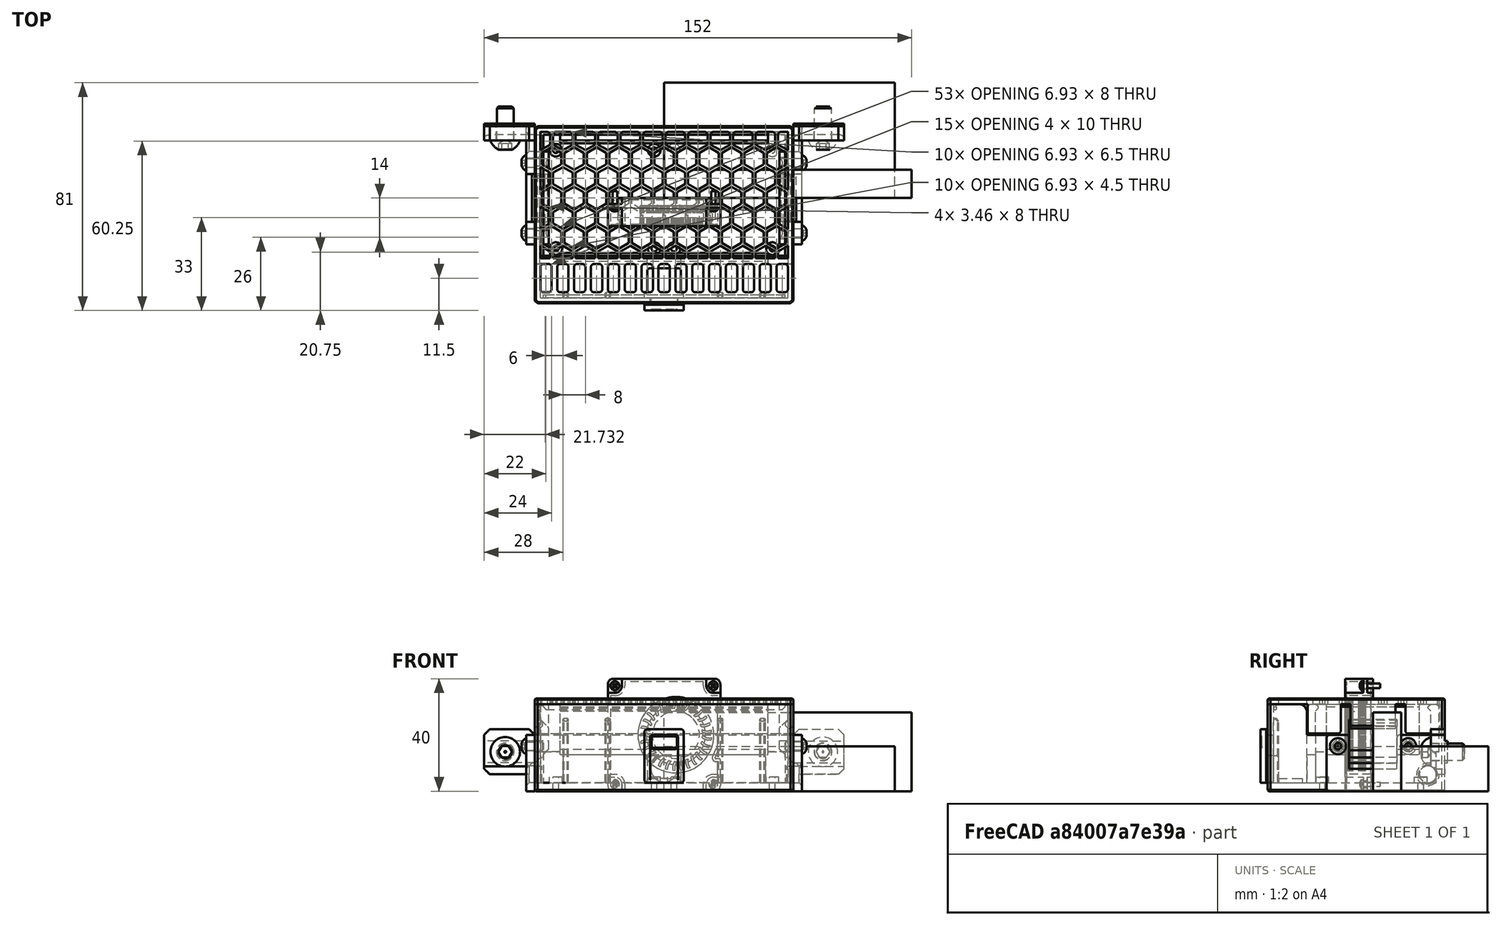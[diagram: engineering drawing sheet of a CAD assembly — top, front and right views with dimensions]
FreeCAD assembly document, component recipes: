
FREECAD ASSEMBLY — COMPONENT RECIPES ("air-filter-assembly-A4")

This assembly document has 8 components, labeled P0..P7 below (a component is one placed body or linked part). 0 of them carry a construction recipe — the FreeCAD feature program that regenerates the part from scratch, quoted from this document or its linked companion documents; the rest are supplied as boundary geometry only. No exploded tour is included for this assembly.
COMPONENT P0 — geometry summary ("ActiveCarbonFoamCartridge"; no construction recipe available for this part):
  bounding box: 88.0 x 28.0 x 10.0 mm
  tessellated surface: 12 triangles
  volume: 24640 mm^3 (100% of its bounding box)
  symmetry: 2-fold rotationally symmetric about the z axis; mirror-symmetric across its y mid-plane, z mid-plane
COMPONENT P1 — geometry summary ("AirFilterHousing"; no construction recipe available for this part):
  bounding box: 92.0 x 63.0 x 31.0 mm
  tessellated surface: 13,756 triangles
  volume: 42470 mm^3 (24% of its bounding box)
COMPONENT P2 — geometry summary ("FilterGrill"; no construction recipe available for this part):
  bounding box: 92.0 x 63.0 x 12.5 mm
  tessellated surface: 9,828 triangles
  volume: 7808 mm^3 (11% of its bounding box)
  symmetry: mirror-symmetric across its x mid-plane
COMPONENT P3 — geometry summary ("HepaFilter"; no construction recipe available for this part):
  bounding box: 82.0 x 41.0 x 16.0 mm
  tessellated surface: 12 triangles
  volume: 53792 mm^3 (100% of its bounding box)
  symmetry: 2-fold rotationally symmetric about the x axis; 2-fold rotationally symmetric about the y axis; mirror-symmetric across its x mid-plane, y mid-plane, z mid-plane
COMPONENT P4 — geometry summary ("Level"; no construction recipe available for this part):
  bounding box: 19.0 x 15.0 x 14.0 mm
  tessellated surface: 2,312 triangles
  volume: 1102 mm^3 (28% of its bounding box)
  symmetry: mirror-symmetric across its x mid-plane
COMPONENT P5 — geometry summary ("MountBracket_Left"; no construction recipe available for this part):
  bounding box: 49.0 x 22.0 x 21.0 mm
  tessellated surface: 23,148 triangles
  volume: 3540 mm^3 (16% of its bounding box)
COMPONENT P6 — geometry summary ("MountBracket_Right"; no construction recipe available for this part):
  bounding box: 49.0 x 22.0 x 21.0 mm
  tessellated surface: 23,148 triangles
  volume: 3540 mm^3 (16% of its bounding box)
COMPONENT P7 — geometry summary ("4010Fan_"; no construction recipe available for this part):
  bounding box: 40.0 x 40.0 x 12.5 mm
  tessellated surface: 27,556 triangles
  volume: 5335 mm^3 (27% of its bounding box)
PROVENANCE & LICENSES
A FreeCAD (.FCStd) document from a public repository crawl; recipes are the document's own serialized feature recipes (and, for linked parts, companion documents' recipes).
License: gpl-3.0.
